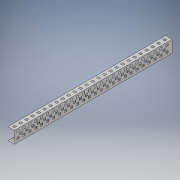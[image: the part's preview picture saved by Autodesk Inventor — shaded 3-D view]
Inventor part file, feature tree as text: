
AUTODESK INVENTOR PART (.ipt)
format: ipt  version: 2018 (Build 220112000, 112)  size: 676,864 bytes
history: native  units: in
note: dims shown in document units (in); Inventor stores cm internally (conversion verified against a paired STEP export)
features: sketch x6, extrude x6
ambient origin geometry x8: Origin, YZ Plane, XZ Plane, XY Plane, X Axis, Y Axis, Z Axis, Center Point
bodies: Solid1 (feature_tree), Solid2 (feature_tree), Solid3 (feature_tree)
feature tree (12):
  sketch  "Sketch1"  dims[d0=0.9449in d1=12.4016in]
  extrude  "Extrusion1"  Depth=12.4016in
  extrude  "Extrusion2"  Depth=12.4016in
  extrude  "Extrusion3"  Depth=0.0039in TaperAngle=0.0deg
  extrude  "Extrusion4"  Depth=12.4016in
  extrude  "Extrusion5"  Depth=0.18in
  extrude  "Extrusion6"  Depth=0.3937in
  sketch  "Sketch2"  dims[d2=0.5118in d3=12.4016in]
  sketch  "Sketch3"  dims[d4=0.0039in d5=0.0in d6=0.0039in d7=0.0in]
  sketch  "Sketch4"  dims[d8=0.5118in d9=12.4016in]
  sketch  "Sketch5"  dims[d10=0.0039in d11=0.0in d12=0.18in]
  sketch  "Sketch6"  dims[d13=0.18in d14=0.3937in d16=1.0in d17=10.2362in d19=0.4724in d21=0.0039in d22=0.0in d23=0.18in d24=0.3937in d26=1.0in d27=10.2362in d29=0.4685in d31=0.0039in d32=0.0in d33=0.18in d34=0.18in d35=10.2362in d37=0.4685in d38=0.7874in d40=0.4724in d43=0.18in d44=0.18in d45=9.8425in d47=0.4685in d48=0.3937in d50=1.0in d52=0.0039in d53=0.0in]
